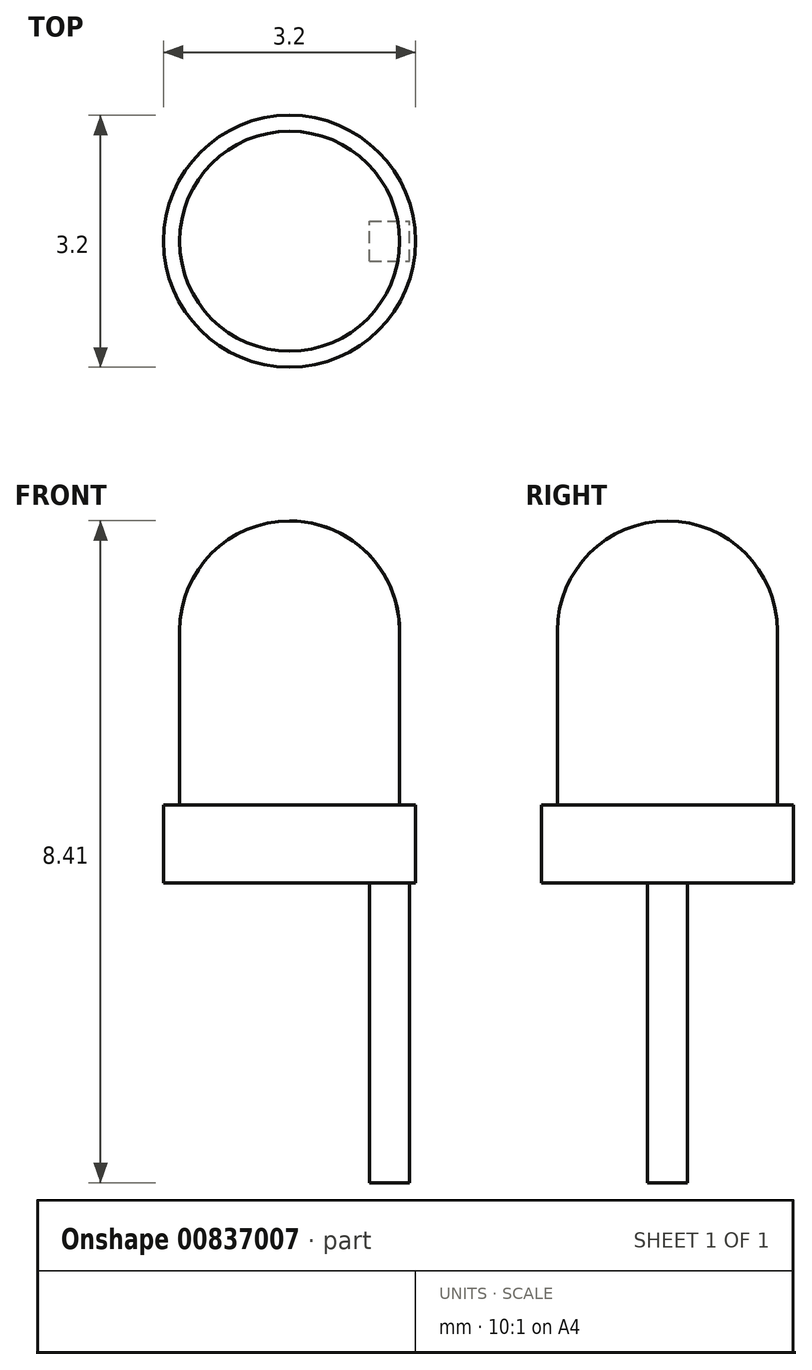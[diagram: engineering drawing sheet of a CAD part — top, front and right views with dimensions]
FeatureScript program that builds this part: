
annotation { "Feature Type Name" : "Feature", "Feature Type Description" : "" }
export const myFeature = defineFeature(function(context is Context, id is Id, definition is map)
    precondition{}
    {
        {
            var Q0;
            Q0=qCreatedBy(makeId("Front.planeOp"),FACE);
            var sketch = newSketch(context, id + "F0", { "sketchPlane" : qUnion([Q0])});
            skLineSegment(sketch, "E0", {"start": v(0, 0) * mm, "end": v(0, 4.6) * mm});
            skLineSegment(sketch, "E1", {"start": v(1.4, 3.2) * mm, "end": v(1.4, 1) * mm});
            skLineSegment(sketch, "E2", {"start": v(1.4, 1) * mm, "end": v(1.6, 1) * mm});
            skLineSegment(sketch, "E3", {"start": v(1.6, 1) * mm, "end": v(1.6, 0) * mm});
            skLineSegment(sketch, "E4", {"start": v(1.6, 0) * mm, "end": v(0, 0) * mm});
            skArc(sketch, "E5", {"start": v(1.4, 3.2) * mm, "mid": v(0.99, 4.19) * mm, "end": v(0, 4.6) * mm});
            skSolve(sketch);
        }
        {
            var Q0;
            Q0 = qSketchRegion(id + "F0", true);
            var Q1;
            Q1=sQuery(id+"F0.wireOp",EDGE,"E0");
            revolve(context, id + "F1", {"surfaceOperationType" : NewSurfaceOperationType.NEW, "entities" : qUnion([Q0]), "axis" : qUnion([Q1]), "revolveType" : RevolveType.FULL});
        }
        {
            var Q0;
            Q0=makeQuery(id+"F1.opRevolve","SWEPT_FACE",FACE,{"disambiguationData":[OSD([sQuery(id+"F0.wireOp",EDGE,"E4")])]});
            var sketch = newSketch(context, id + "F2", { "sketchPlane" : qUnion([Q0])});
            skLineSegment(sketch, "E6.bottom", {"start": v(1.02, 0.25) * mm, "end": v(1.52, 0.25) * mm});
            skLineSegment(sketch, "E6.top", {"start": v(1.02, -0.25) * mm, "end": v(1.52, -0.25) * mm});
            skLineSegment(sketch, "E6.left", {"start": v(1.02, 0.25) * mm, "end": v(1.02, -0.25) * mm});
            skLineSegment(sketch, "E6.right", {"start": v(1.52, 0.25) * mm, "end": v(1.52, -0.25) * mm});
            skLineSegment(sketch, "E7", {"start": v(1.27, 0.25) * mm, "end": v(1.27, -0.25) * mm, "construction": true});
            skLineSegment(sketch, "E8", {"start": v(1.02, 0) * mm, "end": v(1.52, 0) * mm, "construction": true});
            skPoint(sketch, "E9", {"position": v(1.27, 0) * mm});
            skSolve(sketch);
        }
        {
            var Q0;
            Q0 = qSketchRegion(id + "F2", true);
            extrude(context, id + "F3", {"entities" : qUnion([Q0]), "operationType" : NewBodyOperationType.ADD, "depth" : 3.8 * mm, "offsetDistance" : 25.4 * mm});
        }
    });
